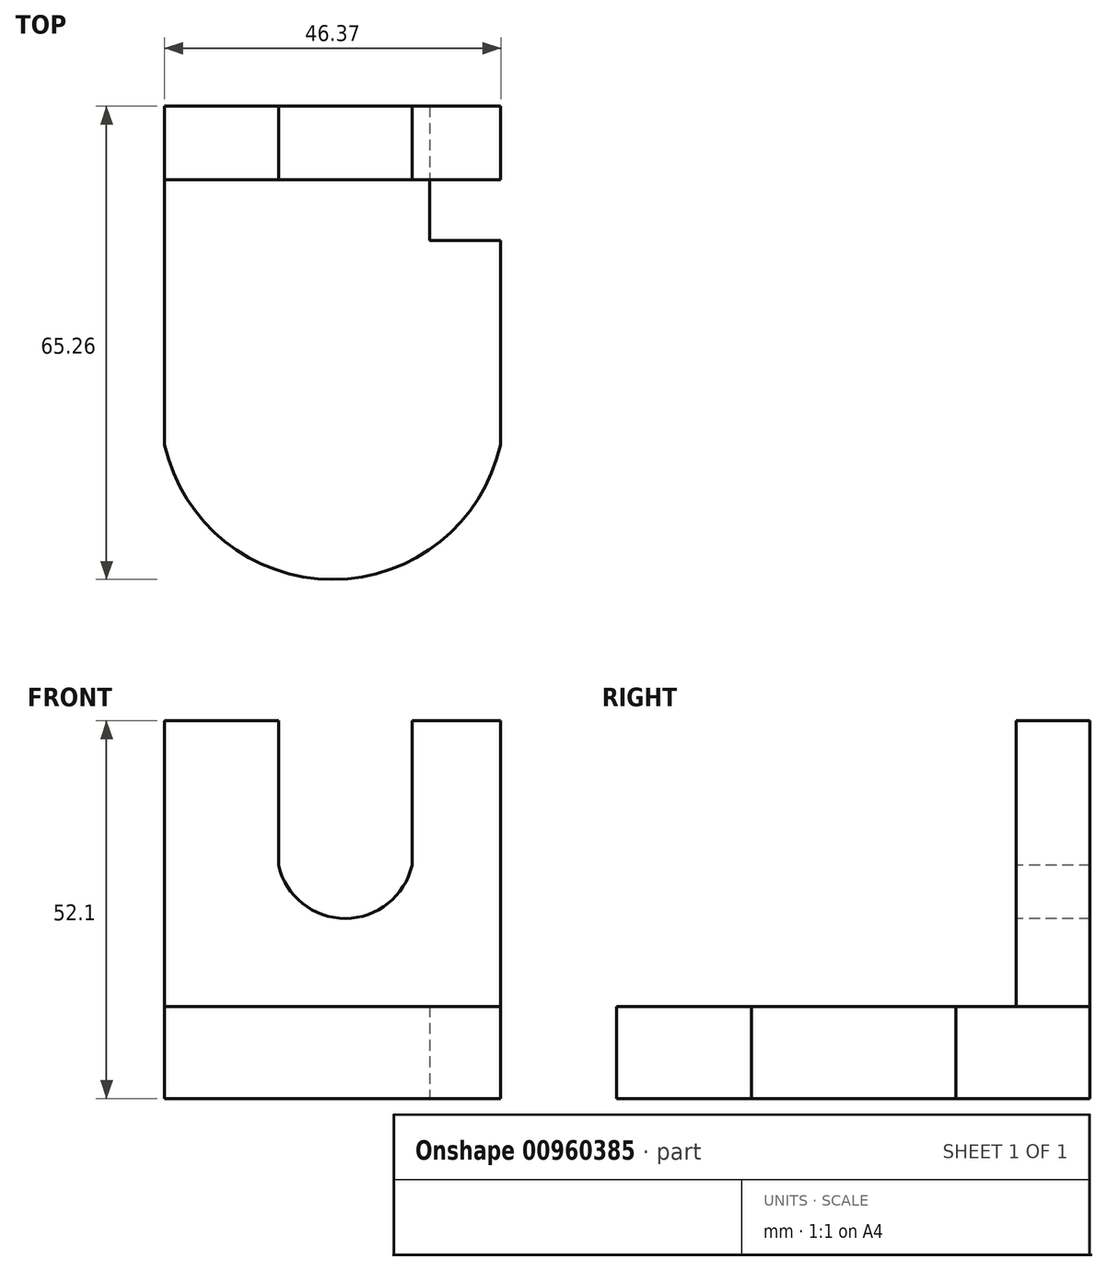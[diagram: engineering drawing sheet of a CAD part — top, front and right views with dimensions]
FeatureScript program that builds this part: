
annotation { "Feature Type Name" : "Feature", "Feature Type Description" : "" }
export const myFeature = defineFeature(function(context is Context, id is Id, definition is map)
    precondition{}
    {
        {
            var Q0;
            Q0=qCreatedBy(makeId("Top.planeOp"),FACE);
            var sketch = newSketch(context, id + "F0", { "sketchPlane" : qUnion([Q0])});
            skLineSegment(sketch, "E0.bottom", {"start": v(-36.55, 27.77) * mm, "end": v(0, 27.77) * mm});
            skLineSegment(sketch, "E0.left", {"start": v(-36.55, 27.77) * mm, "end": v(-36.55, -8.78) * mm});
            skLineSegment(sketch, "E0.right", {"start": v(9.79, 19.43) * mm, "end": v(9.79, -8.78) * mm});
            skArc(sketch, "E1", {"start": v(-36.55, -8.78) * mm, "mid": v(-13.38, -27.33) * mm, "end": v(9.79, -8.78) * mm});
            skLineSegment(sketch, "E2.top", {"start": v(9.79, 19.43) * mm, "end": v(0, 19.43) * mm});
            skLineSegment(sketch, "E2.right", {"start": v(0, 27.77) * mm, "end": v(0, 19.43) * mm});
            skSolve(sketch);
        }
        {
            var Q0;
            Q0=makeQuery(id+"F0.imprint","IMPRINT",FACE,{"disambiguationData":[TD([[makeQuery(id+"F0.imprint","IMPRINT",EDGE,{"derivedFrom":sQuery(id+"F0.wireOp",EDGE,"E0.bottom")}),-1.0]])]});
            extrude(context, id + "F1", {"entities" : qUnion([Q0]), "depth" : 12.7 * mm, "offsetDistance" : 25.4 * mm});
        }
        {
            var Q0;
            Q0=makeQuery(id+"F1.opExtrude","SWEPT_FACE",FACE,{"disambiguationData":[OSD([sQuery(id+"F0.wireOp",EDGE,"E0.bottom")])]});
            var sketch = newSketch(context, id + "F2", { "sketchPlane" : qUnion([Q0])});
            skLineSegment(sketch, "E3.bottom", {"start": v(36.55, 0) * mm, "end": v(0, 0) * mm});
            skLineSegment(sketch, "E3.top", {"start": v(36.55, 52.1) * mm, "end": v(20.84, 52.1) * mm});
            skLineSegment(sketch, "E3.left", {"start": v(36.55, 0) * mm, "end": v(36.55, 52.1) * mm});
            skLineSegment(sketch, "E3.right", {"start": v(-9.82, 12.7) * mm, "end": v(-9.82, 52.1) * mm});
            skLineSegment(sketch, "E4.left", {"start": v(2.42, 52.1) * mm, "end": v(2.42, 32.18) * mm});
            skLineSegment(sketch, "E4.right", {"start": v(20.84, 52.1) * mm, "end": v(20.84, 32.18) * mm});
            skArc(sketch, "E5", {"start": v(2.42, 32.18) * mm, "mid": v(11.63, 24.83) * mm, "end": v(20.84, 32.18) * mm});
            skLineSegment(sketch, "E6.trimOffspring", {"start": v(2.42, 52.1) * mm, "end": v(-9.82, 52.1) * mm});
            skLineSegment(sketch, "E7.bottom", {"start": v(0, 12.7) * mm, "end": v(-9.82, 12.7) * mm});
            skLineSegment(sketch, "E7.left", {"start": v(0, 12.7) * mm, "end": v(0, 0) * mm});
            skSolve(sketch);
        }
        {
            var Q0;
            Q0=qSketchRegion(id+"F2",true);
            extrude(context, id + "F3", {"entities" : qUnion([Q0]), "operationType" : NewBodyOperationType.ADD, "depth" : 10.16 * mm, "offsetDistance" : 25.4 * mm});
        }
    });
